# Revit family: O19021001_Lavamanos San Lorenzo Petit para Incrustar Blanco
name_source: partatom
category: Plumbing Fixtures
units: mm (PartAtom-declared; Revit-internal decimal feet)

## family parameters
Always vertical = Yes
Cut with Voids When Loaded = No
OmniClass Number = 23.31.13.11
OmniClass Title = Single Sinks
Part Type = Normal
Room Calculation Point = No
Round Connector Dimension = Use Diameter
Shared = No
Work Plane-Based = No

## types (1)
- O19021001_Lavamanos San Lorenzo Petit para Incrustar Blanco
    Acabado = Brillante
    Alto = 22 cm
    Ancho = 43.3 cm
    Colección = Lavamanos 2000
    Creado por = IDD
    Dimensión del pozo = 38.5
    Diámetro del desagüe = 44 mm
    Fecha de creación = 03/08/2020
    Forma = Ovalado
    Garantía = Garantía completa para siempre en la porcelana
    Incluye = Tapón de rebose cromado.
    Largo = 33.5 cm
    Línea = San Lorenzo Petit
    Material = Corona_Porcelana_Sanitaria_Blanco
    Materiales = Porcelana sanitaria
    No incluye = Grifería
    Productos compatibles = Grifería monocontrol media, grifería 8 pulgadas
    Profundidad del pozo = 18.5 cm
    Resistencia = Alta resistencia al rayado y cambios de temperatura
    Tecnologías = CoverGloss, Aquaflow
    Tipo de desagüe = Expuesto
    Tipo de instalación = A pared
    Tipo de lavamanos = Para incrustar
    Uso = Residencial

## geometry (parser evidence)
native form markers: Sweep x5
no freeform markers — native parametric forms only
